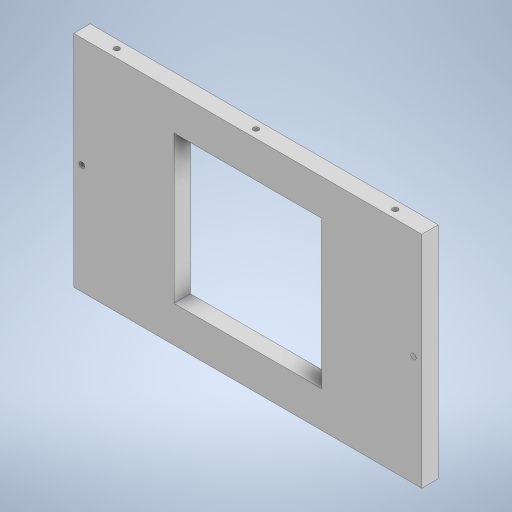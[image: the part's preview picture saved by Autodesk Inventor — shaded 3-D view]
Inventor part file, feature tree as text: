
AUTODESK INVENTOR PART (.ipt)
format: ipt  version: 2023.2 (Build 272271030, 271C)  size: 570,880 bytes
history: native  units: mm
features: extrude x5, sketch x5, projected_geometry x2
ambient origin geometry x8: Origin, YZ Plane, XZ Plane, XY Plane, X Axis, Y Axis, Z Axis, Center Point
bodies: Solid1 (feature_tree)
feature tree (12):
  extrude  "Extrusion1"  Depth=120.0mm
  extrude  "Extrusion2"  Depth=80.5mm
  extrude  "Extrusion3"  Depth=10.0mm TaperAngle=0.0deg
  extrude  "Extrusion4"  Depth=3.0mm
  extrude  "Extrusion5"  Depth=10.0mm TaperAngle=0.0deg
  sketch  "Sketch1"  dims[d0=190.0mm d1=120.0mm]
  sketch  "Sketch2"  dims[d2=9.0mm d3=0.0mm d4=80.5mm]
  projected_geometry  "Projected Loop1"
  sketch  "Sketch3"  dims[d5=80.5mm d6=10.0mm d7=0.0mm]
  projected_geometry  "Projected Loop2"
  sketch  "Sketch4"  dims[d8=3.0mm d9=3.0mm]
  sketch  "Sketch5"  dims[d10=3.0mm d11=10.0mm d12=0.0mm d13=10.0mm d14=0.0mm d15=9.0mm d16=9.0mm d17=3.0mm d18=3.0mm d19=10.0mm d20=0.0mm]
